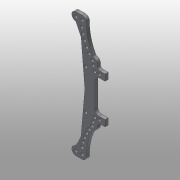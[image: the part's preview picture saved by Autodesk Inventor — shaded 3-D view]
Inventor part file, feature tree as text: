
AUTODESK INVENTOR PART (.ipt)
format: ipt  version: 2015 (Build 190159000, 159)  size: 172,032 bytes
history: native  units: mm
features: other x3, sketch x1
ambient origin geometry x8: Origin, YZ Plane, XZ Plane, XY Plane, X Axis, Y Axis, Z Axis, Center Point
bodies: Solid1 (feature_tree)
feature tree (4):
  other  "500-120.ipt"
  other  "Solid2::500-120.ipt"
  other  "TaggingFeature1"
  sketch  "Sketch1"  dims[d0=10.0mm]
